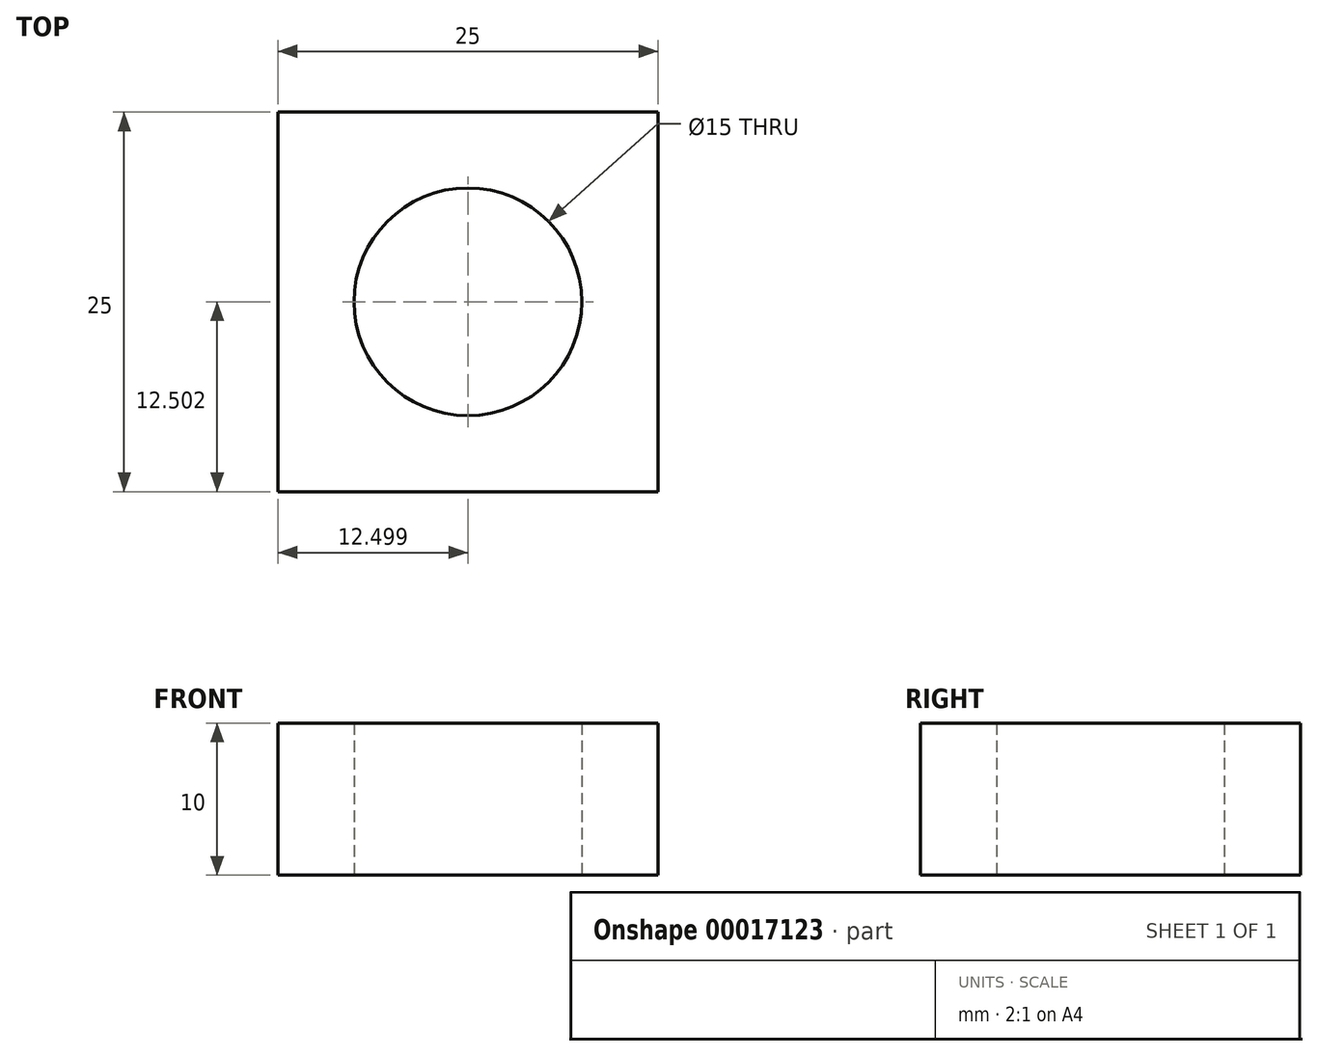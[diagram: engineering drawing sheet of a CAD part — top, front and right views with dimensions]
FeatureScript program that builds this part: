
annotation { "Feature Type Name" : "Feature", "Feature Type Description" : "" }
export const myFeature = defineFeature(function(context is Context, id is Id, definition is map)
    precondition{}
    {
        {
            var Q0;
            Q0=qCreatedBy(makeId("Top.planeOp"),FACE);
            var sketch = newSketch(context, id + "F0", { "sketchPlane" : qUnion([Q0])});
            skLineSegment(sketch, "E0.bottom", {"start": v(-16.08, 9.32) * mm, "end": v(8.92, 9.32) * mm});
            skLineSegment(sketch, "E0.top", {"start": v(-16.08, -15.68) * mm, "end": v(8.92, -15.68) * mm});
            skLineSegment(sketch, "E0.left", {"start": v(-16.08, 9.32) * mm, "end": v(-16.08, -15.68) * mm});
            skLineSegment(sketch, "E0.right", {"start": v(8.92, 9.32) * mm, "end": v(8.92, -15.68) * mm});
            skCircle(sketch, "E1", {"center": v(-3.58, -3.18) * mm, "radius": 7.5 * mm});
            skPoint(sketch, "E2.orphan", {"position": v(-3.58, 9.32) * mm});
            skPoint(sketch, "E3.end.orphan", {"position": v(-3.58, -15.68) * mm});
            skSolve(sketch);
        }
        {
            var Q0;
            Q0 = qSketchRegion(id + "F0", true);
            extrude(context, id + "F1", {"entities" : qUnion([Q0]), "depth" : 10 * mm});
        }
    });
